FCSTD DOCUMENT  (FreeCAD 0.21R33771 (Git))
Label: flex_cable_outline
License: All rights reserved
LicenseURL: https://en.wikipedia.org/wiki/All_rights_reserved
objects: Sketcher::SketchObject×1, Spreadsheet::Sheet×1
note: 1 computed .brp shape members not serialized (recipe doc carries the construction recipe); baked Part::Feature solids carry a one-line shape summary decoded from their .brp

FEATURE [Sketcher::SketchObject] Sketch
  FullyConstrained = false
  expr: Constraints[11] = Spreadsheet.notch / 2
  expr: Constraints[229] = 0.75 / 2 + 0.5
  sketch-geometry (78):
    g0: LineSegment StartX=-30.9649 StartY=6.20769 StartZ=0 EndX=-3.16486 EndY=6.20769 EndZ=0
    g1: LineSegment StartX=-24.6649 StartY=2.20769 StartZ=0 EndX=-30.9649 EndY=2.20769 EndZ=0
    g2: LineSegment StartX=-30.9649 StartY=2.20769 StartZ=0 EndX=-30.9649 EndY=6.20769 EndZ=0
    g3: LineSegment StartX=-24.6649 StartY=2.20769 StartZ=0 EndX=-23.4149 EndY=2.20769 EndZ=0
    g4: ArcOfCircle CenterX=-24.0399 CenterY=2.83769 CenterZ=0 NormalX=0 NormalY=0 NormalZ=1 AngleXU=0 Radius=0.625 StartAngle=2.2048e-08 EndAngle=3.14159
    g5: LineSegment StartX=-24.6649 StartY=2.20769 StartZ=0 EndX=-24.6649 EndY=2.83769 EndZ=0
    g6: LineSegment StartX=-23.4149 StartY=2.20769 StartZ=0 EndX=-23.4149 EndY=2.83769 EndZ=0
    g7: LineSegment StartX=-23.4149 StartY=2.20769 StartZ=0 EndX=-16.4649 EndY=2.20769 EndZ=0
    g8: LineSegment StartX=-16.4649 StartY=2.20769 StartZ=0 EndX=-15.2149 EndY=2.20769 EndZ=0
    g9: LineSegment StartX=-16.4649 StartY=2.20769 StartZ=0 EndX=-16.4649 EndY=2.83769 EndZ=0
    g10: ArcOfCircle CenterX=-15.8399 CenterY=2.83769 CenterZ=0 NormalX=0 NormalY=0 NormalZ=1 AngleXU=0 Radius=0.625 StartAngle=2e-16 EndAngle=3.14159
    g11: LineSegment StartX=-15.2149 StartY=2.20769 StartZ=0 EndX=-15.2149 EndY=2.83769 EndZ=0
    g12: LineSegment StartX=-15.2149 StartY=2.20769 StartZ=0 EndX=-7.21486 EndY=2.20769 EndZ=0
    g13: LineSegment StartX=-7.21486 StartY=2.20769 StartZ=0 EndX=-7.21486 EndY=3.20769 EndZ=0
    g14: LineSegment StartX=-7.21486 StartY=3.20769 StartZ=0 EndX=-2.41486 EndY=3.20769 EndZ=0
    g15: LineSegment StartX=-3.16486 StartY=5.57769 StartZ=0 EndX=-3.16486 EndY=6.20769 EndZ=0
    g16: LineSegment StartX=-2.41486 StartY=5.57769 StartZ=0 EndX=-2.41486 EndY=6.20769 EndZ=0
    g17: ArcOfCircle CenterX=-2.78986 CenterY=6.15202 CenterZ=0 NormalX=0 NormalY=0 NormalZ=1 AngleXU=0 Radius=0.685917 StartAngle=4.13396 EndAngle=5.29082
    g18: LineSegment StartX=-2.41486 StartY=3.20769 StartZ=0 EndX=-2.41486 EndY=2.45769 EndZ=0
    g19: LineSegment StartX=-2.41486 StartY=2.45769 StartZ=0 EndX=-1.66486 EndY=2.45769 EndZ=0
    g20: LineSegment StartX=-1.66486 StartY=2.45769 StartZ=0 EndX=-1.66486 EndY=3.08769 EndZ=0
    g21: LineSegment StartX=-1.66486 StartY=2.45769 StartZ=0 EndX=-0.414861 EndY=2.45769 EndZ=0
    g22: ArcOfCircle CenterX=-1.03986 CenterY=3.08769 CenterZ=0 NormalX=0 NormalY=0 NormalZ=1 AngleXU=0 Radius=0.625 StartAngle=3e-16 EndAngle=3.14159
    g23: LineSegment StartX=-0.414861 StartY=2.45769 StartZ=0 EndX=-0.414861 EndY=3.08769 EndZ=0
    g24: LineSegment StartX=-0.414861 StartY=2.45769 StartZ=0 EndX=6.58514 EndY=2.45769 EndZ=0
    g25: LineSegment StartX=-2.41486 StartY=6.20769 StartZ=0 EndX=-2.41486 EndY=11.2077 EndZ=0
    g26: LineSegment StartX=-2.41486 StartY=11.2077 StartZ=0 EndX=20.5851 EndY=11.2077 EndZ=0
    g27: LineSegment StartX=20.5851 StartY=11.2077 StartZ=0 EndX=20.5851 EndY=8.80769 EndZ=0
    g28: LineSegment StartX=6.58514 StartY=2.45769 StartZ=0 EndX=6.58514 EndY=3.95769 EndZ=0
    g29: LineSegment StartX=6.58514 StartY=3.95769 StartZ=0 EndX=10.7851 EndY=3.95769 EndZ=0
    g30: LineSegment StartX=10.7851 StartY=3.95769 StartZ=0 EndX=10.7851 EndY=-6.54231 EndZ=0
    g31: LineSegment StartX=10.7851 StartY=-6.54231 StartZ=0 EndX=18.5351 EndY=-6.54231 EndZ=0
    g32: LineSegment StartX=18.5351 StartY=-6.54231 StartZ=0 EndX=18.5351 EndY=-2.39231 EndZ=0
    g33: LineSegment StartX=18.5351 StartY=-2.39231 StartZ=0 EndX=16.5351 EndY=-2.39231 EndZ=0
    g34: LineSegment StartX=16.5351 StartY=-2.39231 StartZ=0 EndX=16.5351 EndY=2.45769 EndZ=0
    g35: LineSegment StartX=16.5351 StartY=2.45769 StartZ=0 EndX=16.5351 EndY=3.95769 EndZ=0
    g36: LineSegment StartX=16.5351 StartY=3.95769 StartZ=0 EndX=17.2851 EndY=3.95769 EndZ=0
    g37: LineSegment StartX=17.2851 StartY=3.95769 StartZ=0 EndX=17.2851 EndY=2.45769 EndZ=0
    g38: LineSegment StartX=17.2851 StartY=2.45769 StartZ=0 EndX=20.0351 EndY=2.45769 EndZ=0
    g39: LineSegment StartX=20.0351 StartY=2.45769 StartZ=0 EndX=20.0351 EndY=2.85769 EndZ=0
    g40: LineSegment StartX=20.0351 StartY=2.85769 StartZ=0 EndX=25.0351 EndY=2.85769 EndZ=0
    g41: LineSegment StartX=25.0351 StartY=2.85769 StartZ=0 EndX=25.0351 EndY=2.20769 EndZ=0
    g42: LineSegment StartX=25.0351 StartY=2.20769 StartZ=0 EndX=33.2851 EndY=2.20769 EndZ=0
    g43: LineSegment StartX=33.2851 StartY=2.20769 StartZ=0 EndX=33.2851 EndY=2.83769 EndZ=0
    g44: LineSegment StartX=33.2851 StartY=2.20769 StartZ=0 EndX=34.5351 EndY=2.20769 EndZ=0
    g45: LineSegment StartX=34.5351 StartY=2.20769 StartZ=0 EndX=34.5351 EndY=2.83769 EndZ=0
    g46: ArcOfCircle CenterX=33.9101 CenterY=2.83769 CenterZ=0 NormalX=0 NormalY=0 NormalZ=1 AngleXU=0 Radius=0.625 StartAngle=3e-16 EndAngle=3.14159
    g47: LineSegment StartX=34.5351 StartY=2.20769 StartZ=0 EndX=41.0351 EndY=2.20769 EndZ=0
    g48: ArcOfCircle CenterX=41.6601 CenterY=2.83769 CenterZ=0 NormalX=0 NormalY=0 NormalZ=1 AngleXU=0 Radius=0.625 StartAngle=2e-16 EndAngle=3.14159
    g49: LineSegment StartX=41.0351 StartY=2.20769 StartZ=0 EndX=41.0351 EndY=2.83769 EndZ=0
    g50: LineSegment StartX=41.0351 StartY=2.20769 StartZ=0 EndX=42.2851 EndY=2.20769 EndZ=0
    g51: LineSegment StartX=42.2851 StartY=2.20769 StartZ=0 EndX=42.2851 EndY=2.83769 EndZ=0
    g52: LineSegment StartX=42.2851 StartY=2.20769 StartZ=0 EndX=48.2851 EndY=2.20769 EndZ=0
    g53: LineSegment StartX=48.2851 StartY=2.20769 StartZ=0 EndX=48.2851 EndY=6.20769 EndZ=0
    g54: LineSegment StartX=48.2851 StartY=6.20769 StartZ=0 EndX=20.7851 EndY=6.20769 EndZ=0
    g55: LineSegment StartX=0.585139 StartY=6.20769 StartZ=0 EndX=0.585139 EndY=8.80769 EndZ=0
    g56: LineSegment StartX=1.33514 StartY=5.57769 StartZ=0 EndX=1.33514 EndY=6.20769 EndZ=0
    g57: ArcOfCircle CenterX=0.960139 CenterY=6.12314 CenterZ=0 NormalX=0 NormalY=0 NormalZ=1 AngleXU=0 Radius=0.661922 StartAngle=4.1101 EndAngle=5.31468
    g58: LineSegment StartX=0.585139 StartY=5.57769 StartZ=0 EndX=0.585139 EndY=6.20769 EndZ=0
    g59: LineSegment StartX=20.5851 StartY=8.80769 StartZ=0 EndX=14.1851 EndY=8.80769 EndZ=0
    g60-g63: Circle x4 (B-spline internal-alignment scaffolding for g64; pole/knot coordinates omitted)
    g64: BSplineCurve PolesCount=4 KnotsCount=2 Degree=3 IsPeriodic=0
    g65: GeomPoint X=14.1851 Y=8.80769 Z=0
    g66: GeomPoint X=12.9351 Y=8.80769 Z=0
    g67: GeomPoint X=13.002 Y=9.02467 Z=0
    g68: LineSegment StartX=12.9351 StartY=8.80769 StartZ=0 EndX=9.73514 EndY=8.80769 EndZ=0
    g69: LineSegment StartX=8.48514 StartY=8.80769 StartZ=0 EndX=5.28514 EndY=8.80769 EndZ=0
    g70: LineSegment StartX=0.585139 StartY=8.80769 StartZ=0 EndX=4.03514 EndY=8.80769 EndZ=0
    g71: LineSegment StartX=1.33514 StartY=6.20769 StartZ=0 EndX=19.2851 EndY=6.20769 EndZ=0
    g72: LineSegment StartX=20.7166 StartY=6.20769 StartZ=0 EndX=20.7166 EndY=5.45769 EndZ=0
    g73: LineSegment StartX=20.7166 StartY=5.45769 StartZ=0 EndX=19.9666 EndY=5.45769 EndZ=0
    g74: LineSegment StartX=19.3238 StartY=6.17433 StartZ=0 EndX=19.9666 EndY=5.45769 EndZ=0
    g75: Circle CenterX=-1.53986 CenterY=10.3277 CenterZ=0 NormalX=0 NormalY=0 NormalZ=1 AngleXU=0 Radius=0.375
    g76: BSplineCurve PolesCount=4 KnotsCount=2 Degree=3 IsPeriodic=0
    g77: BSplineCurve PolesCount=4 KnotsCount=2 Degree=3 IsPeriodic=0
  constraints (233):
    c: Coincident(g1,g2)
    c: Coincident(g2,g0)
    c: Horizontal(g0)
    c: Horizontal(g1)
    c: Vertical(g2)
    c: DistanceY(g2,g2) = 4
    c: DistanceX(g1,g1) = 6.3
    c: DistanceX(g0,g0) = 27.8
    c: Horizontal(g3)
    c: Coincident(g3,g1)
    c: DistanceX(g3,g3) = 1.25
    c: Radius(g4) = 0.625
    c: Coincident(g5,g1)
    c: Coincident(g5,g4)
    c: Vertical(g5)
    c: Coincident(g6,g3)
    c: Coincident(g6,g4)
    c: Vertical(g6)
    c: Equal(g6,g5)
    c: DistanceY(g6,g6) = 0.63
    c: Coincident(g7,g6)
    c: Horizontal(g7)
    c: DistanceX(g7,g7) = 6.95
    c: Horizontal(g4,g4)
    c: Horizontal(g8)
    c: DistanceX(g8,g8) = 1.25
    c: Radius(g10) = 0.625
    c: Coincident(g9,g10)
    c: Vertical(g9)
    c: Coincident(g11,g8)
    c: Coincident(g11,g10)
    c: Vertical(g11)
    c: Equal(g11,g9)
    c: DistanceY(g11,g11) = 0.63
    c: Horizontal(g10,g10)
    c: Coincident(g7,g9)
    c: Horizontal(g9,g10)
    c: Angle(g10) = 3.14159
    c: Coincident(g12,g11)
    c: Horizontal(g12)
    c: DistanceX(g12,g12) = 8
    c: Coincident(g13,g12)
    c: Vertical(g13)
    c: DistanceY(g13,g13) = 1
    c: Coincident(g14,g13)
    c: Horizontal(g14)
    c: DistanceX(g14,g14) = 4.8
    c: Vertical(g15)
    c: Vertical(g16)
    c: Equal(g16,g15)
    c: DistanceY(g16,g16) = 0.63
    c: Horizontal(g15,g16)
    c: Horizontal(g15,g16)
    c: DistanceX(g15,g16) = 0.75
    c: Coincident(g0,g15)
    c: Coincident(g17,g15)
    c: Coincident(g17,g16)
    c: Coincident(g18,g14)
    c: Vertical(g18)
    c: DistanceY(g18,g18) = 0.75
    c: Coincident(g19,g18)
    c: Horizontal(g19)
    c: DistanceX(g19,g19) = 0.75
    c: Horizontal(g21)
    c: DistanceX(g21,g21) = 1.25
    c: Radius(g22) = 0.625
    c: Coincident(g20,g22)
    c: Vertical(g20)
    c: Coincident(g23,g21)
    c: Coincident(g23,g22)
    c: Vertical(g23)
    c: Equal(g23,g20)
    c: DistanceY(g23,g23) = 0.63
    c: Horizontal(g22,g22)
    c: Horizontal(g20,g22)
    c: Angle(g22) = 3.14159
    c: Coincident(g20,g19)
    c: Coincident(g24,g23)
    c: Horizontal(g24)
    c: DistanceX(g24,g24) = 7
    c: Coincident(g25,g16)
    c: Vertical(g25)
    c: DistanceY(g25,g25) = 5
    c: Coincident(g26,g25)
    c: Horizontal(g26)
    c: DistanceX(g26,g26) = 23
    c: Coincident(g27,g26)
    c: Vertical(g27)
    c: DistanceY(g27,g27) = 2.4
    c: Coincident(g28,g24)
    c: Vertical(g28)
    c: DistanceY(g28,g28) = 1.5
    c: Coincident(g29,g28)
    c: Horizontal(g29)
    c: DistanceX(g29,g29) = 4.2
    c: Coincident(g30,g29)
    c: Vertical(g30)
    c: DistanceY(g30,g30) = 10.5
    c: Coincident(g31,g30)
    c: Horizontal(g31)
    c: DistanceX(g31,g31) = 7.75
    c: Coincident(g32,g31)
    c: Vertical(g32)
    c: DistanceY(g32,g32) = 4.15
    c: Coincident(g33,g32)
    c: Horizontal(g33)
    c: DistanceX(g33,g33) = 2
    c: Coincident(g34,g33)
    c: Vertical(g34)
    c: Horizontal(g34,g24)
    c: Coincident(g35,g34)
    c: Coincident(g36,g35)
    c: Horizontal(g36)
    c: DistanceX(g36,g36) = 0.75
    c: Coincident(g37,g36)
    c: Vertical(g37)
    c: Coincident(g38,g37)
    c: Horizontal(g38)
    c: DistanceX(g38,g38) = 2.75
    c: Coincident(g39,g38)
    c: Vertical(g39)
    c: DistanceY(g39,g39) = 0.4
    c: Coincident(g40,g39)
    c: Horizontal(g40)
    c: DistanceX(g40,g40) = 5
    c: Coincident(g41,g40)
    c: Vertical(g41)
    c: Horizontal(g12,g41)
    c: Coincident(g42,g41)
    c: Horizontal(g42)
    c: DistanceX(g42,g42) = 8.25
    c: Horizontal(g44)
    c: DistanceX(g44,g44) = 1.25
    c: Radius(g46) = 0.625
    c: Coincident(g43,g46)
    c: Vertical(g43)
    c: Coincident(g45,g44)
    c: Coincident(g45,g46)
    c: Vertical(g45)
    c: Equal(g45,g43)
    c: DistanceY(g45,g45) = 0.63
    c: Horizontal(g46,g46)
    c: Horizontal(g43,g46)
    c: Angle(g46) = 3.14159
    c: Coincident(g43,g42)
    c: Coincident(g47,g45)
    c: Horizontal(g47)
    c: DistanceX(g47,g47) = 6.5
    c: Horizontal(g50)
    c: DistanceX(g50,g50) = 1.25
    c: Radius(g48) = 0.625
    c: Coincident(g49,g48)
    c: Vertical(g49)
    c: Coincident(g51,g50)
    c: Coincident(g51,g48)
    c: Vertical(g51)
    c: Equal(g51,g49)
    c: DistanceY(g51,g51) = 0.63
    c: Horizontal(g48,g48)
    c: Horizontal(g49,g48)
    c: Angle(g48) = 3.14159
    c: Coincident(g49,g47)
    c: Coincident(g52,g51)
    c: Horizontal(g52)
    c: DistanceX(g52,g52) = 6
    c: Coincident(g53,g52)
    c: Vertical(g53)
    c: Equal(g2,g53)
    c: Coincident(g54,g53)
    c: Horizontal(g54)
    c: DistanceX(g54,g54) = 27.5
    c: Vertical(g55)
    c: Horizontal(g16,g55)
    c: DistanceX(g16,g55) = 3
    c: Horizontal(g55,g27)
    c: Vertical(g58)
    c: Vertical(g56)
    c: Equal(g56,g58)
    c: DistanceY(g56,g56) = 0.63
    c: Horizontal(g58,g56)
    c: Horizontal(g58,g56)
    c: DistanceX(g58,g56) = 0.75
    c: Coincident(g57,g58)
    c: Coincident(g57,g56)
    c: Coincident(g58,g55)
    c: Horizontal(g71,g54)
    c: Coincident(g59,g27)
    c: Horizontal(g59)
    c: DistanceX(g59,g59) = 6.4
    c: DistanceX(g64,g59) = 1.25
    c: Weight(g60) = 1
    c: Coincident(g64,g59)
    c: Equal(g60,g61)
    c: Equal(g60,g62)
    c: Equal(g60,g63)
    c: InternalAlignment(g60-g63 -> g64) x4
    c: InternalAlignment(g65,g64)
    c: InternalAlignment(g66,g64)
    c: PointOnObject(g67,g64)
    c: Vertical(g64,g62)
    c: Horizontal(g61,g62)
    c: DistanceY(g64,g62) = 0.6
    c: Coincident(g68,g64)
    c: Horizontal(g68)
    c: DistanceX(g68,g68) = 3.2
    c: Horizontal(g69)
    c: DistanceX(g69,g68) = 1.25
    c: DistanceX(g69,g69) = 3.2
    c: DistanceX(g70,g69) = 1.25
    c: Coincident(g70,g55)
    c: Horizontal(g70)
    c: Vertical(g59,g61)
    c: Horizontal(g64,g59)
    c: Equal(g28,g35)
    c: Horizontal(g34,g37)
    c: Parallel(g35,g37)
    c: DistanceX(g71,g54) = 1.5
    c: Coincident(g71,g56)
    c: PointOnObject(g72,g54)
    c: Vertical(g72)
    c: DistanceY(g72,g72) = 0.75
    c: Coincident(g73,g72)
    c: Horizontal(g73)
    c: DistanceX(g73,g73) = 0.75
    c: Coincident(g74,g73)
    c: Diameter(g75) = 0.75
    c: Distance(g75,g25) = 0.875
    c: Distance(g75,g26) = 0.88
    c: Coincident(g76,g68)
    c: Coincident(g69,g76)
    c: Coincident(g77,g69)
    c: Coincident(g70,g77)
    c: DistanceY(g70,g69) = 0
FEATURE [Spreadsheet::Sheet] Spreadsheet
  cells = A1='notch; B1(notch)=1.25
